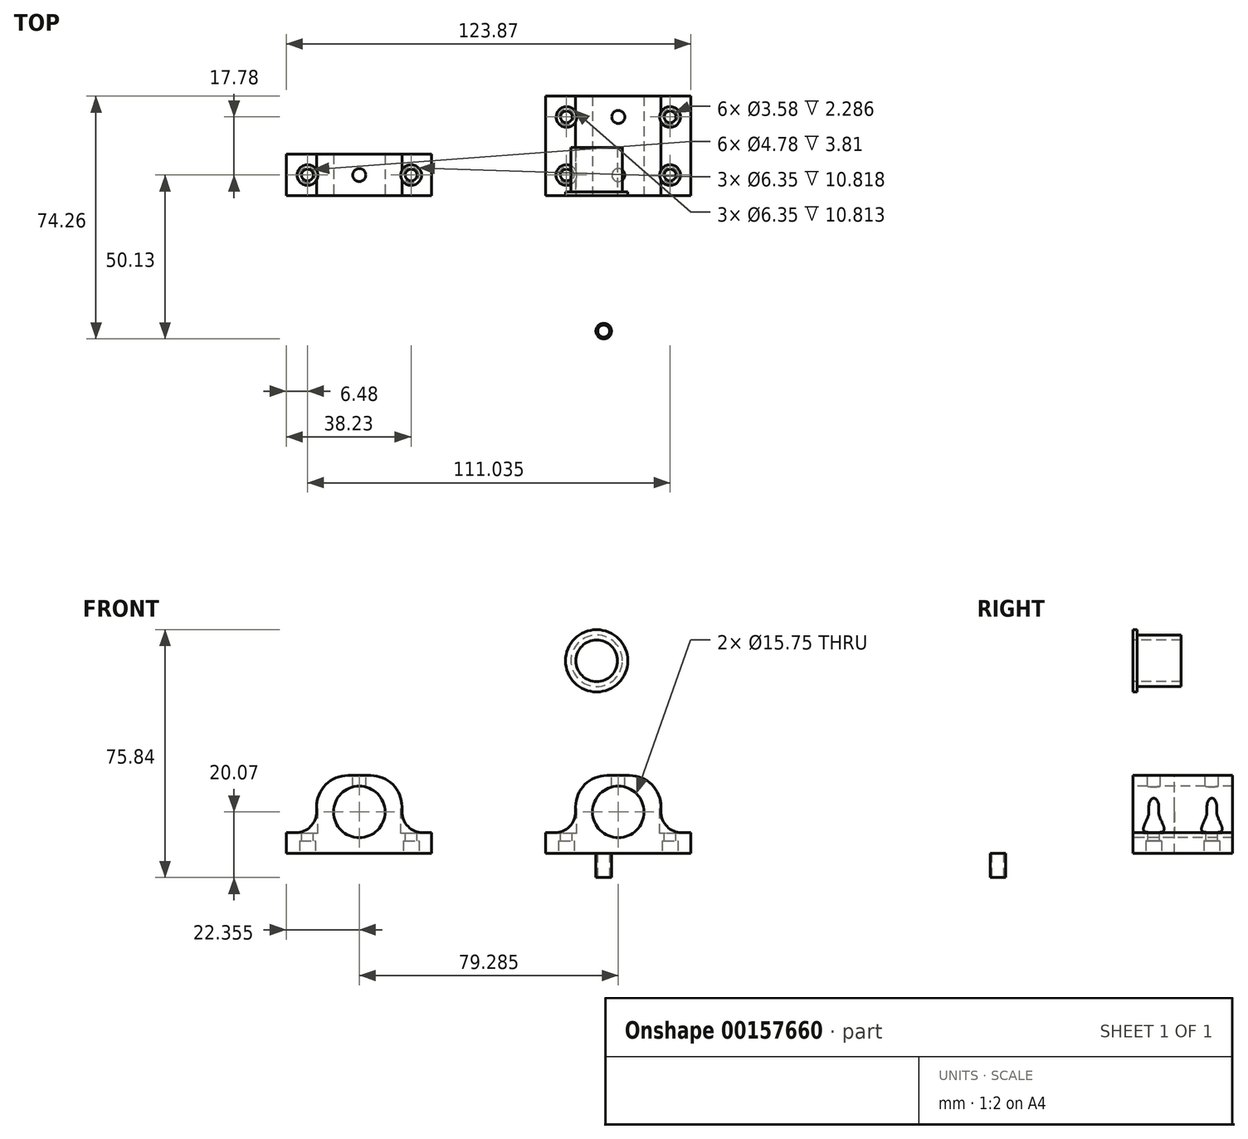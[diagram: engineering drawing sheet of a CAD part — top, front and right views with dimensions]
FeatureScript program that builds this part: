
annotation { "Feature Type Name" : "Feature", "Feature Type Description" : "" }
export const myFeature = defineFeature(function(context is Context, id is Id, definition is map)
    precondition{}
    {
        {
            var Q0;
            Q0=qCreatedBy(makeId("Front.planeOp"),FACE);
            var sketch = newSketch(context, id + "F0", { "sketchPlane" : qUnion([Q0])});
            skLineSegment(sketch, "E0.bottom", {"start": v(-58.25, 0) * mm, "end": v(-13.8, 0) * mm});
            skLineSegment(sketch, "E0.top", {"start": v(-39.32, 23.88) * mm, "end": v(-32.47, 23.88) * mm});
            skLineSegment(sketch, "E0.left", {"start": v(-58.25, 0) * mm, "end": v(-58.25, 6.35) * mm});
            skLineSegment(sketch, "E0.right", {"start": v(-13.8, 0) * mm, "end": v(-13.8, 6.35) * mm});
            skCircle(sketch, "E1", {"center": v(-35.9, 12.7) * mm, "radius": 7.87 * mm});
            skLineSegment(sketch, "E2.bottom", {"start": v(-58.25, 0) * mm, "end": v(-13.8, 0) * mm, "construction": true});
            skLineSegment(sketch, "E2.top", {"start": v(-58.25, 6.35) * mm, "end": v(-48.98, 6.35) * mm, "construction": true});
            skLineSegment(sketch, "E2.left", {"start": v(-58.25, 0) * mm, "end": v(-58.25, 6.35) * mm, "construction": true});
            skLineSegment(sketch, "E2.right", {"start": v(-13.8, 0) * mm, "end": v(-13.8, 6.35) * mm, "construction": true});
            skLineSegment(sketch, "E3.bottom", {"start": v(-22.81, 23.88) * mm, "end": v(-48.98, 23.88) * mm, "construction": true});
            skLineSegment(sketch, "E3.left", {"start": v(-22.81, 23.88) * mm, "end": v(-22.81, 6.35) * mm, "construction": true});
            skLineSegment(sketch, "E3.right", {"start": v(-48.98, 23.88) * mm, "end": v(-48.98, 6.35) * mm, "construction": true});
            skLineSegment(sketch, "E4", {"start": v(-58.25, 6.35) * mm, "end": v(-55.33, 6.35) * mm});
            skLineSegment(sketch, "E5", {"start": v(-48.98, 12.7) * mm, "end": v(-48.98, 14.22) * mm});
            skLineSegment(sketch, "E6", {"start": v(-22.81, 14.22) * mm, "end": v(-22.81, 12.7) * mm});
            skLineSegment(sketch, "E7", {"start": v(-16.46, 6.35) * mm, "end": v(-13.8, 6.35) * mm});
            skPoint(sketch, "E8.orphan", {"position": v(-48.98, 1.52) * mm});
            skPoint(sketch, "E9.orphan", {"position": v(-22.81, 1.52) * mm});
            skLineSegment(sketch, "E10.trimOffspring", {"start": v(-22.81, 6.35) * mm, "end": v(-13.8, 6.35) * mm, "construction": true});
            skPoint(sketch, "E11.visualSharp", {"position": v(-22.81, 6.35) * mm});
            skArc(sketch, "E11.filletArc", {"start": v(-22.81, 12.7) * mm, "mid": v(-20.95, 8.2) * mm, "end": v(-16.46, 6.35) * mm});
            skPoint(sketch, "E12.visualSharp", {"position": v(-48.98, 6.35) * mm});
            skArc(sketch, "E12.filletArc", {"start": v(-55.33, 6.35) * mm, "mid": v(-50.84, 8.2) * mm, "end": v(-48.98, 12.7) * mm});
            skPoint(sketch, "E13.visualSharp", {"position": v(-48.98, 23.88) * mm});
            skArc(sketch, "E13.filletArc", {"start": v(-39.32, 23.88) * mm, "mid": v(-46.15, 21.05) * mm, "end": v(-48.98, 14.22) * mm});
            skPoint(sketch, "E14.visualSharp", {"position": v(-22.81, 23.88) * mm});
            skArc(sketch, "E14.filletArc", {"start": v(-22.81, 14.22) * mm, "mid": v(-25.64, 21.05) * mm, "end": v(-32.47, 23.88) * mm});
            skSolve(sketch);
        }
        {
            var Q0;
            Q0=makeQuery(id+"F0.imprint","IMPRINT",FACE,{"disambiguationData":[TD([[makeQuery(id+"F0.imprint","IMPRINT",EDGE,{"derivedFrom":sQuery(id+"F0.wireOp",EDGE,"E0.bottom")}),1.0]])]});
            extrude(context, id + "F1", {"entities" : qUnion([Q0]), "oppositeDirection" : true, "depth" : 12.7 * mm});
        }
        {
            var Q0;
            Q0=qCreatedBy(makeId("Top.planeOp"),FACE);
            cPlane(context, id + "F2", {"entities" : qUnion([Q0]), "cplaneType" : CPlaneType.OFFSET, "offset" : 23.88 * mm, "width" : 152.4 * mm, "height" : 152.4 * mm});
        }
        {
            var Q0;
            Q0=makeQuery(id+"F1.opExtrude","SWEPT_FACE",FACE,{"disambiguationData":[OSD([sQuery(id+"F0.wireOp",EDGE,"E0.top")])]});
            var sketch = newSketch(context, id + "F3", { "sketchPlane" : qUnion([Q0])});
            skLineSegment(sketch, "E15", {"start": v(-35.9, 0) * mm, "end": v(-35.9, 12.7) * mm, "construction": true});
            skLineSegment(sketch, "E16", {"start": v(-35.9, 6.35) * mm, "end": v(-11.59, 6.35) * mm, "construction": true});
            skLineSegment(sketch, "E17", {"start": v(-11.59, 6.35) * mm, "end": v(-62.35, 6.35) * mm, "construction": true});
            skCircle(sketch, "E18", {"center": v(-51.77, 6.35) * mm, "radius": 3.18 * mm});
            skCircle(sketch, "E19", {"center": v(-20.02, 6.35) * mm, "radius": 3.18 * mm});
            skSolve(sketch);
        }
        {
            var Q0;
            Q0=makeQuery(id+"F3.imprint","IMPRINT",FACE,{"disambiguationData":[TD([[makeQuery(id+"F3.imprint","IMPRINT",EDGE,{"derivedFrom":sQuery(id+"F3.wireOp",EDGE,"E18")}),1.0]])]});
            var Q1;
            Q1=makeQuery(id+"F3.imprint","IMPRINT",FACE,{"disambiguationData":[TD([[makeQuery(id+"F3.imprint","IMPRINT",EDGE,{"derivedFrom":sQuery(id+"F3.wireOp",EDGE,"E19")}),1.0]])]});
            extrude(context, id + "F4", {"entities" : qUnion([Q0, Q1]), "operationType" : NewBodyOperationType.REMOVE, "oppositeDirection" : true, "depth" : 17.78 * mm});
        }
        {
            var Q0;
            Q0=makeQuery(id+"F4.boolean.opBoolean","COPY",FACE,{"derivedFrom":makeQuery(id+"F4.opExtrude","CAP_FACE",FACE,{"disambiguationData":[OSD([sQuery(id+"F3.wireOp",EDGE,"E18")])],"isStart":false})});
            var sketch = newSketch(context, id + "F5", { "sketchPlane" : qUnion([Q0])});
            skCircle(sketch, "E20", {"center": v(-51.77, 6.35) * mm, "radius": 1.8 * mm});
            skSolve(sketch);
        }
        {
            var Q0;
            Q0=makeQuery(id+"F4.boolean.opBoolean","COPY",FACE,{"derivedFrom":makeQuery(id+"F4.opExtrude","CAP_FACE",FACE,{"disambiguationData":[OSD([sQuery(id+"F3.wireOp",EDGE,"E19")])],"isStart":false})});
            var sketch = newSketch(context, id + "F6", { "sketchPlane" : qUnion([Q0])});
            skCircle(sketch, "E21", {"center": v(-20.02, 6.35) * mm, "radius": 1.8 * mm});
            skSolve(sketch);
        }
        {
            var Q0;
            Q0=makeQuery(id+"F5.imprint","IMPRINT",FACE,{"disambiguationData":[TD([[makeQuery(id+"F5.imprint","IMPRINT",EDGE,{"derivedFrom":sQuery(id+"F5.wireOp",EDGE,"E20")}),1.0]])]});
            var Q1;
            Q1=makeQuery(id+"F6.imprint","IMPRINT",FACE,{"disambiguationData":[TD([[makeQuery(id+"F6.imprint","IMPRINT",EDGE,{"derivedFrom":sQuery(id+"F6.wireOp",EDGE,"E21")}),1.0]])]});
            extrude(context, id + "F7", {"entities" : qUnion([Q0, Q1]), "operationType" : NewBodyOperationType.REMOVE, "oppositeDirection" : true, "depth" : 25.4 * mm});
        }
        {
            var Q0;
            Q0=makeQuery(id+"F1.opExtrude","SWEPT_FACE",FACE,{"disambiguationData":[OSD([sQuery(id+"F0.wireOp",EDGE,"E0.bottom")])]});
            var sketch = newSketch(context, id + "F8", { "sketchPlane" : qUnion([Q0])});
            skCircle(sketch, "E22", {"center": v(-51.77, -6.35) * mm, "radius": 2.39 * mm});
            skCircle(sketch, "E23", {"center": v(-20.02, -6.35) * mm, "radius": 2.39 * mm});
            skSolve(sketch);
        }
        {
            var Q0;
            Q0=makeQuery(id+"F8.imprint","IMPRINT",FACE,{"disambiguationData":[TD([[makeQuery(id+"F8.imprint","IMPRINT",EDGE,{"derivedFrom":sQuery(id+"F8.wireOp",EDGE,"E22")}),1.0]])]});
            var Q1;
            Q1=makeQuery(id+"F8.imprint","IMPRINT",FACE,{"disambiguationData":[TD([[makeQuery(id+"F8.imprint","IMPRINT",EDGE,{"derivedFrom":sQuery(id+"F8.wireOp",EDGE,"E23")}),1.0]])]});
            extrude(context, id + "F9", {"entities" : qUnion([Q0, Q1]), "operationType" : NewBodyOperationType.REMOVE, "oppositeDirection" : true, "depth" : 3.8 * mm});
        }
        {
            var Q0;
            Q0=makeQuery(id+"F1.opExtrude","SWEPT_FACE",FACE,{"disambiguationData":[OSD([sQuery(id+"F0.wireOp",EDGE,"E0.top")])]});
            var sketch = newSketch(context, id + "F10", { "sketchPlane" : qUnion([Q0])});
            skCircle(sketch, "E24", {"center": v(-35.9, 6.35) * mm, "radius": 2 * mm});
            skPoint(sketch, "E24.centerSnap0", {"position": v(-35.9, 0) * mm});
            skPoint(sketch, "E24.centerSnap1", {"position": v(-39.32, 6.35) * mm});
            skSolve(sketch);
        }
        {
            var Q0;
            Q0=makeQuery(id+"F10.imprint","IMPRINT",FACE,{"disambiguationData":[TD([[makeQuery(id+"F10.imprint","IMPRINT",EDGE,{"derivedFrom":sQuery(id+"F10.wireOp",EDGE,"E24")}),1.0]])]});
            extrude(context, id + "F11", {"entities" : qUnion([Q0]), "operationType" : NewBodyOperationType.REMOVE, "oppositeDirection" : true, "depth" : 6.35 * mm});
        }
        {
            var Q0;
            Q0=qCreatedBy(makeId("Front.planeOp"),FACE);
            var sketch = newSketch(context, id + "F12", { "sketchPlane" : qUnion([Q0])});
            skLineSegment(sketch, "E25.bottom", {"start": v(21.17, 0) * mm, "end": v(65.62, 0) * mm});
            skLineSegment(sketch, "E25.left", {"start": v(21.17, 0) * mm, "end": v(21.17, 6.35) * mm});
            skLineSegment(sketch, "E25.right", {"start": v(65.62, 0) * mm, "end": v(65.62, 6.35) * mm});
            skLineSegment(sketch, "E26.bottom", {"start": v(21.17, 0) * mm, "end": v(65.62, 0) * mm, "construction": true});
            skLineSegment(sketch, "E26.top", {"start": v(21.17, 6.35) * mm, "end": v(30.3, 6.35) * mm, "construction": true});
            skLineSegment(sketch, "E26.left", {"start": v(21.17, 0) * mm, "end": v(21.17, 6.35) * mm, "construction": true});
            skLineSegment(sketch, "E26.right", {"start": v(65.62, 0) * mm, "end": v(65.62, 6.35) * mm, "construction": true});
            skLineSegment(sketch, "E27.left", {"start": v(56.47, 6.35) * mm, "end": v(56.47, 23.88) * mm, "construction": true});
            skLineSegment(sketch, "E27.right", {"start": v(30.3, 6.35) * mm, "end": v(30.3, 23.88) * mm, "construction": true});
            skLineSegment(sketch, "E28", {"start": v(21.17, 6.35) * mm, "end": v(23.96, 6.35) * mm});
            skLineSegment(sketch, "E29", {"start": v(56.47, 14.22) * mm, "end": v(56.47, 12.7) * mm});
            skLineSegment(sketch, "E30", {"start": v(65.62, 6.35) * mm, "end": v(62.82, 6.35) * mm});
            skLineSegment(sketch, "E31", {"start": v(30.3, 12.7) * mm, "end": v(30.3, 14.22) * mm});
            skLineSegment(sketch, "E32.trimOffspring", {"start": v(56.47, 6.35) * mm, "end": v(65.62, 6.35) * mm, "construction": true});
            skPoint(sketch, "E33.visualSharp", {"position": v(30.3, 6.35) * mm});
            skArc(sketch, "E33.filletArc", {"start": v(23.96, 6.35) * mm, "mid": v(28.45, 8.2) * mm, "end": v(30.3, 12.7) * mm});
            skPoint(sketch, "E34.visualSharp", {"position": v(56.47, 6.35) * mm});
            skArc(sketch, "E34.filletArc", {"start": v(56.47, 12.7) * mm, "mid": v(58.33, 8.2) * mm, "end": v(62.82, 6.35) * mm});
            skLineSegment(sketch, "E35", {"start": v(39.96, 23.88) * mm, "end": v(46.82, 23.88) * mm});
            skPoint(sketch, "E36.visualSharp", {"position": v(30.3, 23.88) * mm});
            skArc(sketch, "E36.filletArc", {"start": v(39.96, 23.88) * mm, "mid": v(33.14, 21.05) * mm, "end": v(30.3, 14.22) * mm});
            skPoint(sketch, "E37.visualSharp", {"position": v(56.47, 23.88) * mm});
            skArc(sketch, "E37.filletArc", {"start": v(56.47, 14.22) * mm, "mid": v(53.64, 21.05) * mm, "end": v(46.82, 23.88) * mm});
            skCircle(sketch, "E38", {"center": v(43.4, 12.7) * mm, "radius": 7.87 * mm});
            skPoint(sketch, "E38.centerSnap0", {"position": v(43.4, 0) * mm});
            skSolve(sketch);
        }
        {
            var Q0;
            Q0=makeQuery(id+"F12.imprint","IMPRINT",FACE,{"disambiguationData":[TD([[makeQuery(id+"F12.imprint","IMPRINT",EDGE,{"derivedFrom":sQuery(id+"F12.wireOp",EDGE,"E25.bottom")}),1.0]])]});
            extrude(context, id + "F13", {"entities" : qUnion([Q0]), "oppositeDirection" : true, "depth" : 30.48 * mm});
        }
        {
            var Q0;
            Q0=makeQuery(id+"F13.opExtrude","SWEPT_FACE",FACE,{"disambiguationData":[OSD([sQuery(id+"F12.wireOp",EDGE,"E35")])]});
            var sketch = newSketch(context, id + "F14", { "sketchPlane" : qUnion([Q0])});
            skLineSegment(sketch, "E39.bottom", {"start": v(59.27, 6.35) * mm, "end": v(27.52, 6.35) * mm, "construction": true});
            skLineSegment(sketch, "E39.top", {"start": v(59.27, 24.13) * mm, "end": v(27.52, 24.13) * mm, "construction": true});
            skLineSegment(sketch, "E39.left", {"start": v(59.27, 6.35) * mm, "end": v(59.27, 24.13) * mm, "construction": true});
            skLineSegment(sketch, "E39.right", {"start": v(27.52, 6.35) * mm, "end": v(27.52, 24.13) * mm, "construction": true});
            skPoint(sketch, "E39.middle", {"position": v(43.4, 15.24) * mm});
            skPoint(sketch, "E39.middle.positionSnap0", {"position": v(43.4, 0) * mm});
            skPoint(sketch, "E39.centerSnap0", {"position": v(43.4, 0) * mm});
            skCircle(sketch, "E40", {"center": v(27.52, 6.35) * mm, "radius": 1.8 * mm});
            skCircle(sketch, "E41", {"center": v(27.52, 24.13) * mm, "radius": 1.8 * mm});
            skCircle(sketch, "E42", {"center": v(59.27, 24.13) * mm, "radius": 1.8 * mm});
            skCircle(sketch, "E43", {"center": v(59.27, 6.35) * mm, "radius": 1.8 * mm});
            skCircle(sketch, "E44", {"center": v(27.52, 6.35) * mm, "radius": 3.18 * mm});
            skCircle(sketch, "E45", {"center": v(27.52, 24.13) * mm, "radius": 3.18 * mm});
            skCircle(sketch, "E46", {"center": v(59.27, 24.13) * mm, "radius": 3.18 * mm});
            skCircle(sketch, "E47", {"center": v(59.27, 6.35) * mm, "radius": 3.18 * mm});
            skCircle(sketch, "E48", {"center": v(43.4, 6.35) * mm, "radius": 2 * mm});
            skCircle(sketch, "E49", {"center": v(43.4, 24.13) * mm, "radius": 2 * mm});
            skSolve(sketch);
        }
        {
            var Q0;
            Q0=makeQuery(id+"F14.imprint","IMPRINT",FACE,{"disambiguationData":[TD([[makeQuery(id+"F14.imprint","IMPRINT",EDGE,{"derivedFrom":sQuery(id+"F14.wireOp",EDGE,"E40")}),1.0]])]});
            var Q1;
            Q1=makeQuery(id+"F14.imprint","IMPRINT",FACE,{"disambiguationData":[TD([[makeQuery(id+"F14.imprint","IMPRINT",EDGE,{"derivedFrom":sQuery(id+"F14.wireOp",EDGE,"E41")}),1.0]])]});
            var Q2;
            Q2=makeQuery(id+"F14.imprint","IMPRINT",FACE,{"disambiguationData":[TD([[makeQuery(id+"F14.imprint","IMPRINT",EDGE,{"derivedFrom":sQuery(id+"F14.wireOp",EDGE,"E42")}),1.0]])]});
            var Q3;
            Q3=makeQuery(id+"F14.imprint","IMPRINT",FACE,{"disambiguationData":[TD([[makeQuery(id+"F14.imprint","IMPRINT",EDGE,{"derivedFrom":sQuery(id+"F14.wireOp",EDGE,"E43")}),1.0]])]});
            extrude(context, id + "F15", {"entities" : qUnion([Q0, Q1, Q2, Q3]), "operationType" : NewBodyOperationType.REMOVE, "endBound" : BoundingType.THROUGH_ALL, "oppositeDirection" : true, "depth" : 25.4 * mm});
        }
        {
            var Q0;
            Q0=makeQuery(id+"F14.imprint","IMPRINT",FACE,{"disambiguationData":[TD([[makeQuery(id+"F14.imprint","IMPRINT",EDGE,{"derivedFrom":sQuery(id+"F14.wireOp",EDGE,"E48")}),1.0]])]});
            var Q1;
            Q1=makeQuery(id+"F14.imprint","IMPRINT",FACE,{"disambiguationData":[TD([[makeQuery(id+"F14.imprint","IMPRINT",EDGE,{"derivedFrom":sQuery(id+"F14.wireOp",EDGE,"E49")}),1.0]])]});
            extrude(context, id + "F16", {"entities" : qUnion([Q0, Q1]), "operationType" : NewBodyOperationType.REMOVE, "oppositeDirection" : true, "depth" : 12.7 * mm});
        }
        {
            var Q0;
            Q0=makeQuery(id+"F14.imprint","IMPRINT",FACE,{"disambiguationData":[TD([[makeQuery(id+"F14.imprint","IMPRINT",EDGE,{"derivedFrom":sQuery(id+"F14.wireOp",EDGE,"E40")}),-1.0]])]});
            var Q1;
            Q1=makeQuery(id+"F14.imprint","IMPRINT",FACE,{"disambiguationData":[TD([[makeQuery(id+"F14.imprint","IMPRINT",EDGE,{"derivedFrom":sQuery(id+"F14.wireOp",EDGE,"E41")}),-1.0]])]});
            var Q2;
            Q2=makeQuery(id+"F14.imprint","IMPRINT",FACE,{"disambiguationData":[TD([[makeQuery(id+"F14.imprint","IMPRINT",EDGE,{"derivedFrom":sQuery(id+"F14.wireOp",EDGE,"E43")}),-1.0]])]});
            var Q3;
            Q3=makeQuery(id+"F14.imprint","IMPRINT",FACE,{"disambiguationData":[TD([[makeQuery(id+"F14.imprint","IMPRINT",EDGE,{"derivedFrom":sQuery(id+"F14.wireOp",EDGE,"E42")}),-1.0]])]});
            extrude(context, id + "F17", {"entities" : qUnion([Q0, Q1, Q2, Q3]), "operationType" : NewBodyOperationType.REMOVE, "oppositeDirection" : true, "depth" : 17.78 * mm});
        }
        {
            var Q0;
            Q0=makeQuery(id+"F13.opExtrude","SWEPT_FACE",FACE,{"disambiguationData":[OSD([sQuery(id+"F12.wireOp",EDGE,"E25.bottom")])]});
            var sketch = newSketch(context, id + "F18", { "sketchPlane" : qUnion([Q0])});
            skCircle(sketch, "E50", {"center": v(27.52, -6.35) * mm, "radius": 2.39 * mm});
            skCircle(sketch, "E51", {"center": v(27.52, -24.13) * mm, "radius": 2.39 * mm});
            skCircle(sketch, "E52", {"center": v(59.27, -24.13) * mm, "radius": 2.39 * mm});
            skCircle(sketch, "E53", {"center": v(59.27, -6.35) * mm, "radius": 2.39 * mm});
            skSolve(sketch);
        }
        {
            var Q0;
            Q0=makeQuery(id+"F18.imprint","IMPRINT",FACE,{"disambiguationData":[TD([[makeQuery(id+"F18.imprint","IMPRINT",EDGE,{"derivedFrom":sQuery(id+"F18.wireOp",EDGE,"E50")}),1.0]])]});
            var Q1;
            Q1=makeQuery(id+"F18.imprint","IMPRINT",FACE,{"disambiguationData":[TD([[makeQuery(id+"F18.imprint","IMPRINT",EDGE,{"derivedFrom":sQuery(id+"F18.wireOp",EDGE,"E53")}),1.0]])]});
            var Q2;
            Q2=makeQuery(id+"F18.imprint","IMPRINT",FACE,{"disambiguationData":[TD([[makeQuery(id+"F18.imprint","IMPRINT",EDGE,{"derivedFrom":sQuery(id+"F18.wireOp",EDGE,"E52")}),1.0]])]});
            var Q3;
            Q3=makeQuery(id+"F18.imprint","IMPRINT",FACE,{"disambiguationData":[TD([[makeQuery(id+"F18.imprint","IMPRINT",EDGE,{"derivedFrom":sQuery(id+"F18.wireOp",EDGE,"E51")}),1.0]])]});
            extrude(context, id + "F19", {"entities" : qUnion([Q0, Q1, Q2, Q3]), "operationType" : NewBodyOperationType.REMOVE, "oppositeDirection" : true, "depth" : 3.8 * mm});
        }
        {
            var Q0;
            Q0=qCreatedBy(makeId("Top.planeOp"),FACE);
            var sketch = newSketch(context, id + "F20", { "sketchPlane" : qUnion([Q0])});
            skCircle(sketch, "E54", {"center": v(38.94, -41.4) * mm, "radius": 1.83 * mm});
            skCircle(sketch, "E55", {"center": v(38.94, -41.4) * mm, "radius": 2.38 * mm});
            skSolve(sketch);
        }
        {
            var Q0;
            Q0=makeQuery(id+"F20.imprint","IMPRINT",FACE,{"disambiguationData":[TD([[makeQuery(id+"F20.imprint","IMPRINT",EDGE,{"derivedFrom":sQuery(id+"F20.wireOp",EDGE,"E54")}),-1.0]])]});
            extrude(context, id + "F21", {"entities" : qUnion([Q0]), "oppositeDirection" : true, "depth" : 7.37 * mm});
        }
        {
            var Q0;
            Q0=qCreatedBy(makeId("Front.planeOp"),FACE);
            var sketch = newSketch(context, id + "F22", { "sketchPlane" : qUnion([Q0])});
            skCircle(sketch, "E56", {"center": v(36.78, 58.94) * mm, "radius": 9.53 * mm});
            skCircle(sketch, "E57", {"center": v(36.78, 58.94) * mm, "radius": 6.36 * mm});
            skSolve(sketch);
        }
        {
            var Q0;
            Q0=makeQuery(id+"F22.imprint","IMPRINT",FACE,{"disambiguationData":[TD([[makeQuery(id+"F22.imprint","IMPRINT",EDGE,{"derivedFrom":sQuery(id+"F22.wireOp",EDGE,"E56")}),1.0]])]});
            extrude(context, id + "F23", {"entities" : qUnion([Q0]), "oppositeDirection" : true, "depth" : 1.22 * mm});
        }
        {
            var Q0;
            Q0=makeQuery(id+"F23.opExtrude","CAP_FACE",FACE,{"disambiguationData":[OSD([sQuery(id+"F22.wireOp",EDGE,"E56"),sQuery(id+"F22.wireOp",EDGE,"E57")])],"isStart":false});
            var sketch = newSketch(context, id + "F24", { "sketchPlane" : qUnion([Q0])});
            skCircle(sketch, "E58", {"center": v(-36.78, 58.94) * mm, "radius": 7.88 * mm});
            skSolve(sketch);
        }
        {
            var Q0;
            Q0=makeQuery(id+"F24.imprint","IMPRINT",FACE,{"disambiguationData":[TD([[makeQuery(id+"F24.imprint","IMPRINT",EDGE,{"derivedFrom":sQuery(id+"F24.wireOp",EDGE,"E58")}),1.0]])]});
            extrude(context, id + "F25", {"entities" : qUnion([Q0]), "operationType" : NewBodyOperationType.ADD, "depth" : 13.5 * mm});
        }
    });
